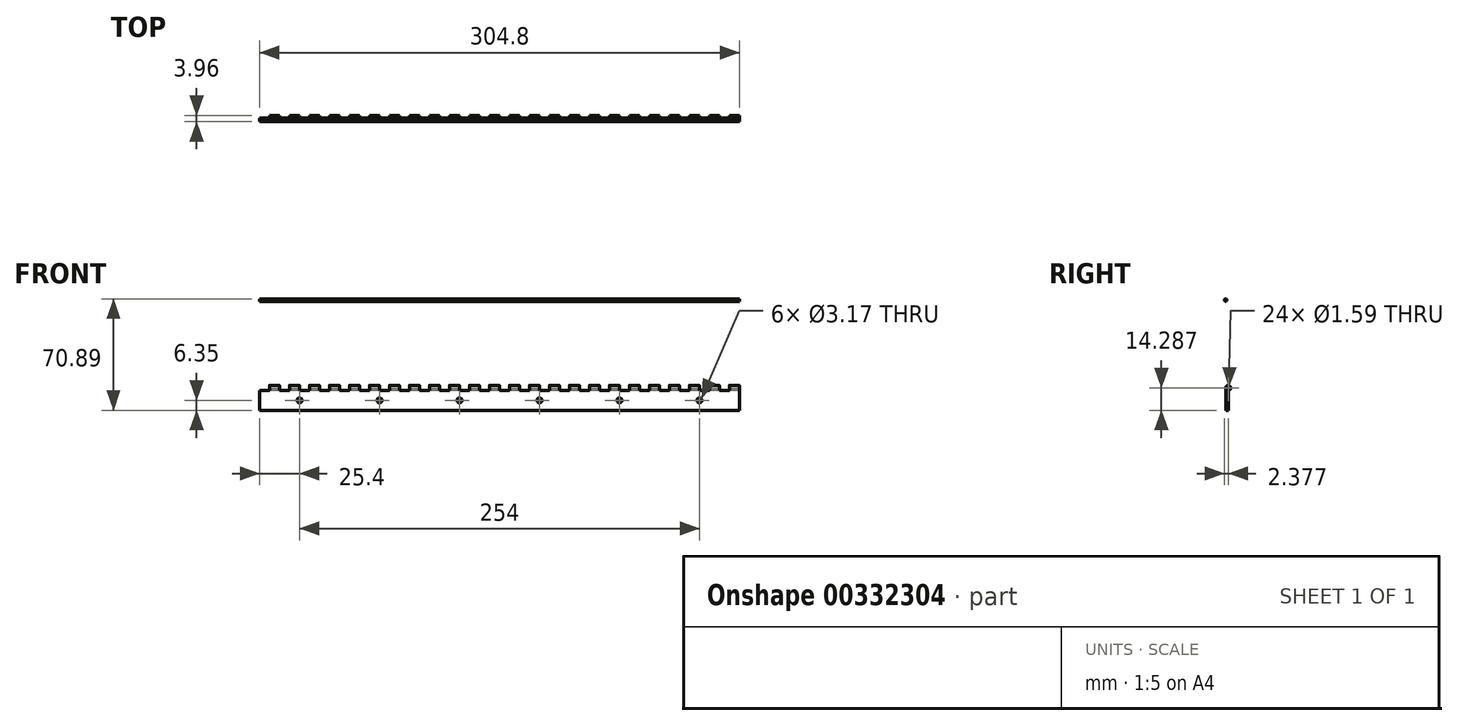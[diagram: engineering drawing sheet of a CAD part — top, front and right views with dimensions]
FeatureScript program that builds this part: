
annotation { "Feature Type Name" : "Feature", "Feature Type Description" : "" }
export const myFeature = defineFeature(function(context is Context, id is Id, definition is map)
    precondition{}
    {
        {
            var Q0;
            Q0=qCreatedBy(makeId("Right.planeOp"),FACE);
            var sketch = newSketch(context, id + "F0", { "sketchPlane" : qUnion([Q0])});
            skLineSegment(sketch, "E0", {"start": v(0, 0) * mm, "end": v(0, 14.29) * mm});
            skLineSegment(sketch, "E1", {"start": v(1.59, 0) * mm, "end": v(0, 0) * mm});
            skArc(sketch, "E2", {"start": v(1.59, 12.7) * mm, "mid": v(2.71, 15.41) * mm, "end": v(0, 14.29) * mm});
            skCircle(sketch, "E3", {"center": v(1.59, 14.29) * mm, "radius": 0.8 * mm});
            skLineSegment(sketch, "E4.trimOffspring", {"start": v(1.59, 12.7) * mm, "end": v(1.59, 0) * mm});
            skSolve(sketch);
        }
        {
            var Q0;
            Q0=makeQuery(id+"F0.imprint","IMPRINT",FACE,{"disambiguationData":[TD([[makeQuery(id+"F0.imprint","IMPRINT",EDGE,{"derivedFrom":sQuery(id+"F0.wireOp",EDGE,"E0")}),-1.0]])]});
            extrude(context, id + "F1", {"entities" : qUnion([Q0]), "depth" : 304.8 * mm});
        }
        {
            var Q0;
            Q0=makeQuery(id+"F1.opExtrude","SWEPT_FACE",FACE,{"disambiguationData":[OSD([sQuery(id+"F0.wireOp",EDGE,"E0")])]});
            var sketch = newSketch(context, id + "F2", { "sketchPlane" : qUnion([Q0])});
            skLineSegment(sketch, "E5", {"start": v(0, 0) * mm, "end": v(0, 12.7) * mm, "construction": true});
            skLineSegment(sketch, "E6.bottom", {"start": v(0, 12.7) * mm, "end": v(6.35, 12.7) * mm});
            skLineSegment(sketch, "E6.top", {"start": v(0, 16.28) * mm, "end": v(6.35, 16.28) * mm});
            skLineSegment(sketch, "E6.left", {"start": v(0, 12.7) * mm, "end": v(0, 16.28) * mm});
            skLineSegment(sketch, "E6.right", {"start": v(6.35, 12.7) * mm, "end": v(6.35, 16.28) * mm});
            skLineSegment(sketch, "E7", {"start": v(6.35, 12.7) * mm, "end": v(12.7, 12.7) * mm, "construction": true});
            skLineSegment(sketch, "E8.1.0.0", {"start": v(12.7, 12.7) * mm, "end": v(19.05, 12.7) * mm});
            skLineSegment(sketch, "E8.1.0.1", {"start": v(12.7, 12.7) * mm, "end": v(12.7, 16.28) * mm});
            skLineSegment(sketch, "E8.1.0.2", {"start": v(12.7, 16.28) * mm, "end": v(19.05, 16.28) * mm});
            skLineSegment(sketch, "E8.1.0.3", {"start": v(19.05, 12.7) * mm, "end": v(19.05, 16.28) * mm});
            skLineSegment(sketch, "E8.1.0.4", {"start": v(19.05, 12.7) * mm, "end": v(25.4, 12.7) * mm, "construction": true});
            skLineSegment(sketch, "E8.2.0.0", {"start": v(25.4, 12.7) * mm, "end": v(31.75, 12.7) * mm});
            skLineSegment(sketch, "E8.2.0.1", {"start": v(25.4, 12.7) * mm, "end": v(25.4, 16.28) * mm});
            skLineSegment(sketch, "E8.2.0.2", {"start": v(25.4, 16.28) * mm, "end": v(31.75, 16.28) * mm});
            skLineSegment(sketch, "E8.2.0.3", {"start": v(31.75, 12.7) * mm, "end": v(31.75, 16.28) * mm});
            skLineSegment(sketch, "E8.2.0.4", {"start": v(31.75, 12.7) * mm, "end": v(38.1, 12.7) * mm, "construction": true});
            skLineSegment(sketch, "E8.direction1", {"start": v(0, 12.7) * mm, "end": v(12.7, 12.7) * mm, "construction": true});
            skLineSegment(sketch, "E9.1.0.0", {"start": v(38.1, 16.28) * mm, "end": v(44.45, 16.28) * mm});
            skLineSegment(sketch, "E9.1.0.1", {"start": v(38.1, 12.7) * mm, "end": v(44.45, 12.7) * mm});
            skLineSegment(sketch, "E9.1.0.2", {"start": v(38.1, 12.7) * mm, "end": v(38.1, 16.28) * mm});
            skLineSegment(sketch, "E9.1.0.3", {"start": v(44.45, 12.7) * mm, "end": v(44.45, 16.28) * mm});
            skLineSegment(sketch, "E9.direction1", {"start": v(25.4, 16.28) * mm, "end": v(38.1, 16.28) * mm, "construction": true});
            skLineSegment(sketch, "E10.0.2.0", {"start": v(50.8, 16.28) * mm, "end": v(57.15, 16.28) * mm});
            skLineSegment(sketch, "E10.3.2.0", {"start": v(50.8, 12.7) * mm, "end": v(57.15, 12.7) * mm});
            skLineSegment(sketch, "E10.6.2.0", {"start": v(50.8, 12.7) * mm, "end": v(50.8, 16.28) * mm});
            skLineSegment(sketch, "E10.9.2.0", {"start": v(57.15, 12.7) * mm, "end": v(57.15, 16.28) * mm});
            skLineSegment(sketch, "E10.0.3.0", {"start": v(63.5, 16.28) * mm, "end": v(69.85, 16.28) * mm});
            skLineSegment(sketch, "E10.3.3.0", {"start": v(63.5, 12.7) * mm, "end": v(69.85, 12.7) * mm});
            skLineSegment(sketch, "E10.6.3.0", {"start": v(63.5, 12.7) * mm, "end": v(63.5, 16.28) * mm});
            skLineSegment(sketch, "E10.9.3.0", {"start": v(69.85, 12.7) * mm, "end": v(69.85, 16.28) * mm});
            skLineSegment(sketch, "E10.0.4.0", {"start": v(76.2, 16.28) * mm, "end": v(82.55, 16.28) * mm});
            skLineSegment(sketch, "E10.3.4.0", {"start": v(76.2, 12.7) * mm, "end": v(82.55, 12.7) * mm});
            skLineSegment(sketch, "E10.6.4.0", {"start": v(76.2, 12.7) * mm, "end": v(76.2, 16.28) * mm});
            skLineSegment(sketch, "E10.9.4.0", {"start": v(82.55, 12.7) * mm, "end": v(82.55, 16.28) * mm});
            skLineSegment(sketch, "E10.0.5.0", {"start": v(88.9, 16.28) * mm, "end": v(95.25, 16.28) * mm});
            skLineSegment(sketch, "E10.3.5.0", {"start": v(88.9, 12.7) * mm, "end": v(95.25, 12.7) * mm});
            skLineSegment(sketch, "E10.6.5.0", {"start": v(88.9, 12.7) * mm, "end": v(88.9, 16.28) * mm});
            skLineSegment(sketch, "E10.9.5.0", {"start": v(95.25, 12.7) * mm, "end": v(95.25, 16.28) * mm});
            skLineSegment(sketch, "E10.0.6.0", {"start": v(101.6, 16.28) * mm, "end": v(107.95, 16.28) * mm});
            skLineSegment(sketch, "E10.3.6.0", {"start": v(101.6, 12.7) * mm, "end": v(107.95, 12.7) * mm});
            skLineSegment(sketch, "E10.6.6.0", {"start": v(101.6, 12.7) * mm, "end": v(101.6, 16.28) * mm});
            skLineSegment(sketch, "E10.9.6.0", {"start": v(107.95, 12.7) * mm, "end": v(107.95, 16.28) * mm});
            skLineSegment(sketch, "E10.0.7.0", {"start": v(114.3, 16.28) * mm, "end": v(120.65, 16.28) * mm});
            skLineSegment(sketch, "E10.3.7.0", {"start": v(114.3, 12.7) * mm, "end": v(120.65, 12.7) * mm});
            skLineSegment(sketch, "E10.6.7.0", {"start": v(114.3, 12.7) * mm, "end": v(114.3, 16.28) * mm});
            skLineSegment(sketch, "E10.9.7.0", {"start": v(120.65, 12.7) * mm, "end": v(120.65, 16.28) * mm});
            skLineSegment(sketch, "E10.0.8.0", {"start": v(127, 16.28) * mm, "end": v(133.35, 16.28) * mm});
            skLineSegment(sketch, "E10.3.8.0", {"start": v(127, 12.7) * mm, "end": v(133.35, 12.7) * mm});
            skLineSegment(sketch, "E10.6.8.0", {"start": v(127, 12.7) * mm, "end": v(127, 16.28) * mm});
            skLineSegment(sketch, "E10.9.8.0", {"start": v(133.35, 12.7) * mm, "end": v(133.35, 16.28) * mm});
            skLineSegment(sketch, "E10.0.9.0", {"start": v(139.7, 16.28) * mm, "end": v(146.05, 16.28) * mm});
            skLineSegment(sketch, "E10.3.9.0", {"start": v(139.7, 12.7) * mm, "end": v(146.05, 12.7) * mm});
            skLineSegment(sketch, "E10.6.9.0", {"start": v(139.7, 12.7) * mm, "end": v(139.7, 16.28) * mm});
            skLineSegment(sketch, "E10.9.9.0", {"start": v(146.05, 12.7) * mm, "end": v(146.05, 16.28) * mm});
            skLineSegment(sketch, "E11.0.10.0", {"start": v(152.4, 16.28) * mm, "end": v(158.75, 16.28) * mm});
            skLineSegment(sketch, "E11.3.10.0", {"start": v(152.4, 12.7) * mm, "end": v(158.75, 12.7) * mm});
            skLineSegment(sketch, "E11.6.10.0", {"start": v(152.4, 12.7) * mm, "end": v(152.4, 16.28) * mm});
            skLineSegment(sketch, "E11.9.10.0", {"start": v(158.75, 12.7) * mm, "end": v(158.75, 16.28) * mm});
            skLineSegment(sketch, "E11.0.11.0", {"start": v(165.1, 16.28) * mm, "end": v(171.45, 16.28) * mm});
            skLineSegment(sketch, "E11.3.11.0", {"start": v(165.1, 12.7) * mm, "end": v(171.45, 12.7) * mm});
            skLineSegment(sketch, "E11.6.11.0", {"start": v(165.1, 12.7) * mm, "end": v(165.1, 16.28) * mm});
            skLineSegment(sketch, "E11.9.11.0", {"start": v(171.45, 12.7) * mm, "end": v(171.45, 16.28) * mm});
            skLineSegment(sketch, "E11.0.12.0", {"start": v(177.8, 16.28) * mm, "end": v(184.15, 16.28) * mm});
            skLineSegment(sketch, "E11.3.12.0", {"start": v(177.8, 12.7) * mm, "end": v(184.15, 12.7) * mm});
            skLineSegment(sketch, "E11.6.12.0", {"start": v(177.8, 12.7) * mm, "end": v(177.8, 16.28) * mm});
            skLineSegment(sketch, "E11.9.12.0", {"start": v(184.15, 12.7) * mm, "end": v(184.15, 16.28) * mm});
            skLineSegment(sketch, "E11.0.13.0", {"start": v(190.5, 16.28) * mm, "end": v(196.85, 16.28) * mm});
            skLineSegment(sketch, "E11.3.13.0", {"start": v(190.5, 12.7) * mm, "end": v(196.85, 12.7) * mm});
            skLineSegment(sketch, "E11.6.13.0", {"start": v(190.5, 12.7) * mm, "end": v(190.5, 16.28) * mm});
            skLineSegment(sketch, "E11.9.13.0", {"start": v(196.85, 12.7) * mm, "end": v(196.85, 16.28) * mm});
            skLineSegment(sketch, "E11.0.14.0", {"start": v(203.2, 16.28) * mm, "end": v(209.55, 16.28) * mm});
            skLineSegment(sketch, "E11.3.14.0", {"start": v(203.2, 12.7) * mm, "end": v(209.55, 12.7) * mm});
            skLineSegment(sketch, "E11.6.14.0", {"start": v(203.2, 12.7) * mm, "end": v(203.2, 16.28) * mm});
            skLineSegment(sketch, "E11.9.14.0", {"start": v(209.55, 12.7) * mm, "end": v(209.55, 16.28) * mm});
            skLineSegment(sketch, "E11.0.15.0", {"start": v(215.9, 16.28) * mm, "end": v(222.25, 16.28) * mm});
            skLineSegment(sketch, "E11.3.15.0", {"start": v(215.9, 12.7) * mm, "end": v(222.25, 12.7) * mm});
            skLineSegment(sketch, "E11.6.15.0", {"start": v(215.9, 12.7) * mm, "end": v(215.9, 16.28) * mm});
            skLineSegment(sketch, "E11.9.15.0", {"start": v(222.25, 12.7) * mm, "end": v(222.25, 16.28) * mm});
            skLineSegment(sketch, "E11.0.16.0", {"start": v(228.6, 16.28) * mm, "end": v(234.95, 16.28) * mm});
            skLineSegment(sketch, "E11.3.16.0", {"start": v(228.6, 12.7) * mm, "end": v(234.95, 12.7) * mm});
            skLineSegment(sketch, "E11.6.16.0", {"start": v(228.6, 12.7) * mm, "end": v(228.6, 16.28) * mm});
            skLineSegment(sketch, "E11.9.16.0", {"start": v(234.95, 12.7) * mm, "end": v(234.95, 16.28) * mm});
            skLineSegment(sketch, "E11.0.17.0", {"start": v(241.3, 16.28) * mm, "end": v(247.65, 16.28) * mm});
            skLineSegment(sketch, "E11.3.17.0", {"start": v(241.3, 12.7) * mm, "end": v(247.65, 12.7) * mm});
            skLineSegment(sketch, "E11.6.17.0", {"start": v(241.3, 12.7) * mm, "end": v(241.3, 16.28) * mm});
            skLineSegment(sketch, "E11.9.17.0", {"start": v(247.65, 12.7) * mm, "end": v(247.65, 16.28) * mm});
            skLineSegment(sketch, "E11.0.18.0", {"start": v(254, 16.28) * mm, "end": v(260.35, 16.28) * mm});
            skLineSegment(sketch, "E11.3.18.0", {"start": v(254, 12.7) * mm, "end": v(260.35, 12.7) * mm});
            skLineSegment(sketch, "E11.6.18.0", {"start": v(254, 12.7) * mm, "end": v(254, 16.28) * mm});
            skLineSegment(sketch, "E11.9.18.0", {"start": v(260.35, 12.7) * mm, "end": v(260.35, 16.28) * mm});
            skLineSegment(sketch, "E11.0.19.0", {"start": v(266.7, 16.28) * mm, "end": v(273.05, 16.28) * mm});
            skLineSegment(sketch, "E11.3.19.0", {"start": v(266.7, 12.7) * mm, "end": v(273.05, 12.7) * mm});
            skLineSegment(sketch, "E11.6.19.0", {"start": v(266.7, 12.7) * mm, "end": v(266.7, 16.28) * mm});
            skLineSegment(sketch, "E11.9.19.0", {"start": v(273.05, 12.7) * mm, "end": v(273.05, 16.28) * mm});
            skLineSegment(sketch, "E12.0.20.0", {"start": v(279.4, 16.28) * mm, "end": v(285.75, 16.28) * mm});
            skLineSegment(sketch, "E12.3.20.0", {"start": v(279.4, 12.7) * mm, "end": v(285.75, 12.7) * mm});
            skLineSegment(sketch, "E12.6.20.0", {"start": v(279.4, 12.7) * mm, "end": v(279.4, 16.28) * mm});
            skLineSegment(sketch, "E12.9.20.0", {"start": v(285.75, 12.7) * mm, "end": v(285.75, 16.28) * mm});
            skLineSegment(sketch, "E12.0.21.0", {"start": v(292.1, 16.28) * mm, "end": v(298.45, 16.28) * mm});
            skLineSegment(sketch, "E12.3.21.0", {"start": v(292.1, 12.7) * mm, "end": v(298.45, 12.7) * mm});
            skLineSegment(sketch, "E12.6.21.0", {"start": v(292.1, 12.7) * mm, "end": v(292.1, 16.28) * mm});
            skLineSegment(sketch, "E12.9.21.0", {"start": v(298.45, 12.7) * mm, "end": v(298.45, 16.28) * mm});
            skLineSegment(sketch, "E12.0.22.0", {"start": v(304.8, 16.28) * mm, "end": v(311.15, 16.28) * mm});
            skLineSegment(sketch, "E12.3.22.0", {"start": v(304.8, 12.7) * mm, "end": v(311.15, 12.7) * mm});
            skLineSegment(sketch, "E12.6.22.0", {"start": v(304.8, 12.7) * mm, "end": v(304.8, 16.28) * mm});
            skLineSegment(sketch, "E12.9.22.0", {"start": v(311.15, 12.7) * mm, "end": v(311.15, 16.28) * mm});
            skLineSegment(sketch, "E12.0.23.0", {"start": v(317.5, 16.28) * mm, "end": v(323.85, 16.28) * mm});
            skLineSegment(sketch, "E12.3.23.0", {"start": v(317.5, 12.7) * mm, "end": v(323.85, 12.7) * mm});
            skLineSegment(sketch, "E12.6.23.0", {"start": v(317.5, 12.7) * mm, "end": v(317.5, 16.28) * mm});
            skLineSegment(sketch, "E12.9.23.0", {"start": v(323.85, 12.7) * mm, "end": v(323.85, 16.28) * mm});
            skLineSegment(sketch, "E12.0.24.0", {"start": v(330.2, 16.28) * mm, "end": v(336.55, 16.28) * mm});
            skLineSegment(sketch, "E12.3.24.0", {"start": v(330.2, 12.7) * mm, "end": v(336.55, 12.7) * mm});
            skLineSegment(sketch, "E12.6.24.0", {"start": v(330.2, 12.7) * mm, "end": v(330.2, 16.28) * mm});
            skLineSegment(sketch, "E12.9.24.0", {"start": v(336.55, 12.7) * mm, "end": v(336.55, 16.28) * mm});
            skSolve(sketch);
        }
        {
            var Q0;
            Q0=qSketchRegion(id+"F2",true);
            extrude(context, id + "F3", {"entities" : qUnion([Q0]), "operationType" : NewBodyOperationType.REMOVE, "endBound" : BoundingType.THROUGH_ALL, "oppositeDirection" : true, "depth" : 25.4 * mm});
        }
        {
            var Q0;
            Q0=qCreatedBy(makeId("Right.planeOp"),FACE);
            var sketch = newSketch(context, id + "F4", { "sketchPlane" : qUnion([Q0])});
            skCircle(sketch, "E13", {"center": v(0, 70.1) * mm, "radius": 0.8 * mm});
            skSolve(sketch);
        }
        {
            var Q0;
            Q0=makeQuery(id+"F4.imprint","IMPRINT",FACE,{"disambiguationData":[TD([[makeQuery(id+"F4.imprint","IMPRINT",EDGE,{"derivedFrom":sQuery(id+"F4.wireOp",EDGE,"E13")}),1.0]])]});
            extrude(context, id + "F5", {"entities" : qUnion([Q0]), "depth" : 304.8 * mm});
        }
        {
            var Q0;
            Q0=makeQuery(id+"F1.opExtrude","SWEPT_FACE",FACE,{"disambiguationData":[OSD([sQuery(id+"F0.wireOp",EDGE,"E0")])]});
            var sketch = newSketch(context, id + "F6", { "sketchPlane" : qUnion([Q0])});
            skLineSegment(sketch, "E14", {"start": v(0, 0) * mm, "end": v(0, 23.46) * mm, "construction": true});
            skPoint(sketch, "E14.endSnap0", {"position": v(0, 6.35) * mm});
            skLineSegment(sketch, "E15.0", {"start": v(25.4, 0) * mm, "end": v(25.4, 23.46) * mm, "construction": true});
            skLineSegment(sketch, "E16.0", {"start": v(76.2, 0) * mm, "end": v(76.2, 23.46) * mm, "construction": true});
            skLineSegment(sketch, "E17.0", {"start": v(127, 0) * mm, "end": v(127, 23.46) * mm, "construction": true});
            skLineSegment(sketch, "E18.0", {"start": v(177.8, 0) * mm, "end": v(177.8, 23.46) * mm, "construction": true});
            skLineSegment(sketch, "E19.0", {"start": v(228.6, 0) * mm, "end": v(228.6, 23.46) * mm, "construction": true});
            skLineSegment(sketch, "E20.0", {"start": v(279.4, 0) * mm, "end": v(279.4, 23.46) * mm, "construction": true});
            skLineSegment(sketch, "E21", {"start": v(0, 0) * mm, "end": v(0, 6.35) * mm, "construction": true});
            skLineSegment(sketch, "E22", {"start": v(0, 6.35) * mm, "end": v(318.84, 6.35) * mm, "construction": true});
            skCircle(sketch, "E23", {"center": v(25.4, 6.35) * mm, "radius": 1.59 * mm});
            skCircle(sketch, "E24", {"center": v(76.2, 6.35) * mm, "radius": 1.59 * mm});
            skCircle(sketch, "E25", {"center": v(127, 6.35) * mm, "radius": 1.59 * mm});
            skCircle(sketch, "E26", {"center": v(177.8, 6.35) * mm, "radius": 1.59 * mm});
            skCircle(sketch, "E27", {"center": v(228.6, 6.35) * mm, "radius": 1.59 * mm});
            skCircle(sketch, "E28", {"center": v(279.4, 6.35) * mm, "radius": 1.59 * mm});
            skSolve(sketch);
        }
        {
            var Q0;
            Q0=qSketchRegion(id+"F6",true);
            extrude(context, id + "F7", {"entities" : qUnion([Q0]), "operationType" : NewBodyOperationType.REMOVE, "endBound" : BoundingType.THROUGH_ALL, "oppositeDirection" : true, "depth" : 25.4 * mm});
        }
    });
